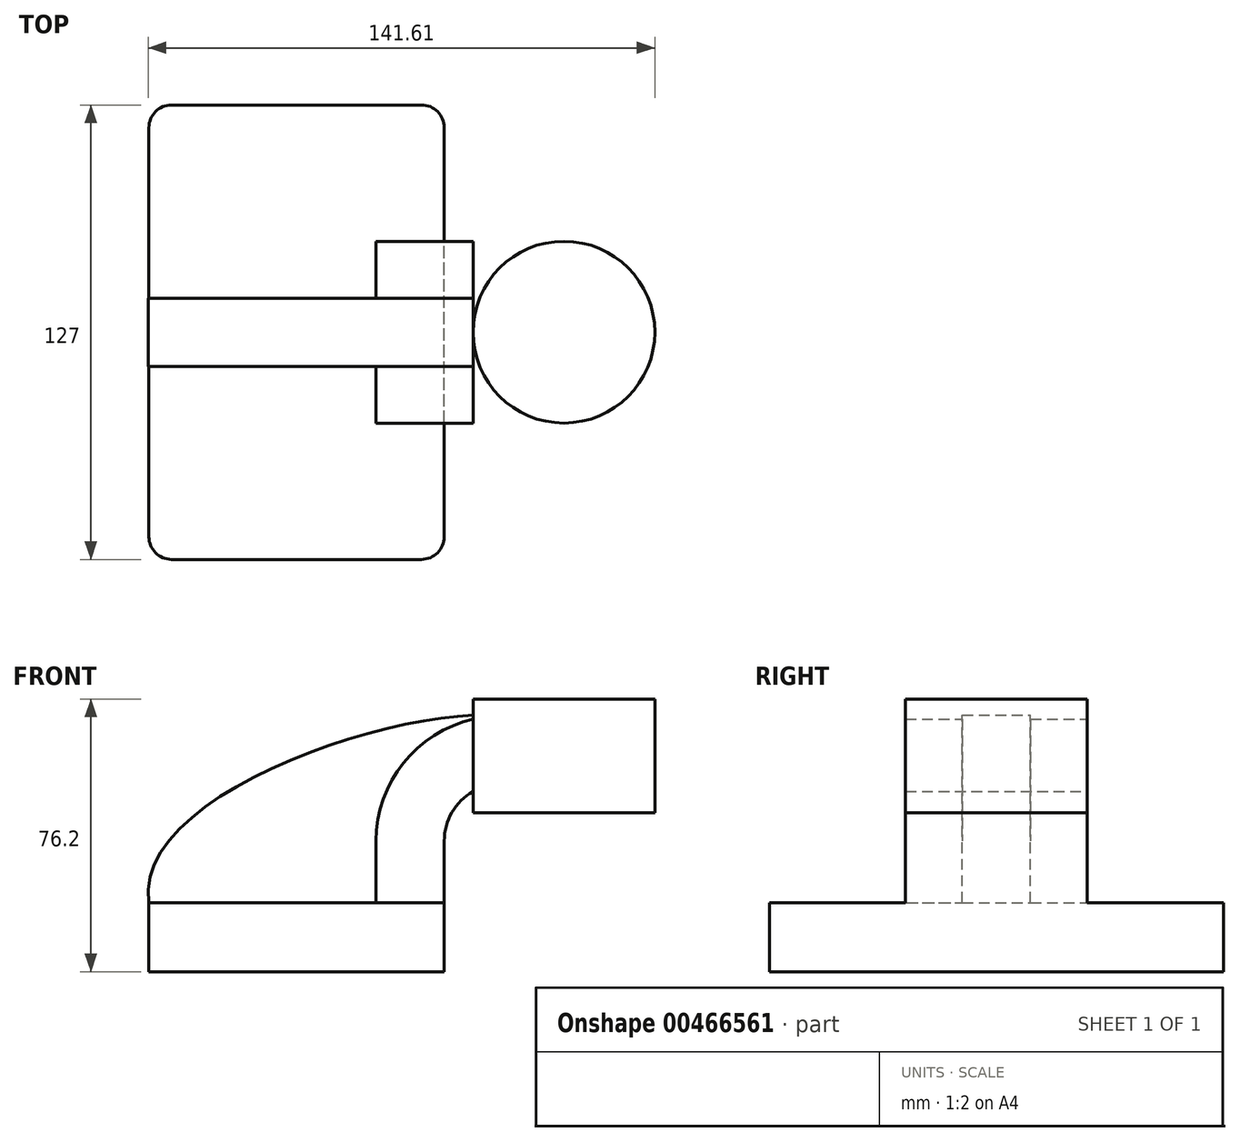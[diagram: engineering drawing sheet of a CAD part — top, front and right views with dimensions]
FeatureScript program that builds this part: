
annotation { "Feature Type Name" : "Feature", "Feature Type Description" : "" }
export const myFeature = defineFeature(function(context is Context, id is Id, definition is map)
    precondition{}
    {
        {
            var Q0;
            Q0=qCreatedBy(makeId("Front.planeOp"),FACE);
            var sketch = newSketch(context, id + "F0", { "sketchPlane" : qUnion([Q0])});
            skLineSegment(sketch, "E0.bottom", {"start": v(-41.28, 9.65) * mm, "end": v(41.27, 9.65) * mm});
            skLineSegment(sketch, "E0.top", {"start": v(-41.28, -9.65) * mm, "end": v(41.28, -9.65) * mm});
            skLineSegment(sketch, "E0.left", {"start": v(-41.28, 9.65) * mm, "end": v(-41.27, -9.65) * mm});
            skLineSegment(sketch, "E0.right", {"start": v(41.28, 9.65) * mm, "end": v(41.28, -9.65) * mm});
            skPoint(sketch, "E0.middle", {"position": v(0, 0) * mm});
            skLineSegment(sketch, "E1", {"start": v(41.27, 9.65) * mm, "end": v(41.27, 26.87) * mm});
            skLineSegment(sketch, "E2.bottom", {"start": v(49.31, 34.8) * mm, "end": v(100.11, 34.8) * mm});
            skLineSegment(sketch, "E2.top", {"start": v(49.31, 66.55) * mm, "end": v(100.11, 66.55) * mm});
            skLineSegment(sketch, "E2.left", {"start": v(49.31, 34.8) * mm, "end": v(49.31, 66.55) * mm});
            skLineSegment(sketch, "E2.right", {"start": v(100.11, 34.8) * mm, "end": v(100.11, 66.55) * mm});
            skPoint(sketch, "E2.middle", {"position": v(74.71, 50.67) * mm});
            skArc(sketch, "E3", {"start": v(41.27, 26.87) * mm, "mid": v(45.92, 38.1) * mm, "end": v(57.15, 42.75) * mm});
            skLineSegment(sketch, "E4", {"start": v(57.15, 42.75) * mm, "end": v(70.79, 42.75) * mm});
            skLineSegment(sketch, "E5.0", {"start": v(57.15, 61.8) * mm, "end": v(70.79, 61.8) * mm});
            skArc(sketch, "E5.1", {"start": v(22.22, 26.87) * mm, "mid": v(32.45, 51.57) * mm, "end": v(57.15, 61.8) * mm});
            skLineSegment(sketch, "E5.2", {"start": v(22.22, 9.65) * mm, "end": v(22.22, 26.87) * mm});
            skLineSegment(sketch, "E6", {"start": v(74.71, 34.8) * mm, "end": v(74.71, 66.55) * mm});
            skFitSpline(sketch, "E7", {"points": [v(-41.28, 9.65) * mm, v(57.15, 61.8) * mm], "startDerivative": vector(-14.58, 91.77) * mm, "endDerivative": vector(82.09, -9.41) * mm});
            skLineSegment(sketch, "E8", {"start": v(70.79, 61.8) * mm, "end": v(70.79, 42.75) * mm});
            skSolve(sketch);
        }
        {
            var Q0;
            Q0=makeQuery(id+"F0.imprint","IMPRINT",FACE,{"disambiguationData":[TD([[makeQuery(id+"F0.imprint","IMPRINT",EDGE,{"derivedFrom":sQuery(id+"F0.wireOp",EDGE,"E0.top")}),1.0]])]});
            extrude(context, id + "F1", {"entities" : qUnion([Q0]), "endBound" : BoundingType.SYMMETRIC, "depth" : 127 * mm});
        }
        {
            var Q0;
            {var subQ1=sQuery(id+"F0.wireOp",EDGE,"E1");Q0=makeQuery(id+"F0.imprint","IMPRINT",FACE,{"disambiguationData":[TD([[makeQuery(id+"F0.imprint","IMPRINT",EDGE,{"derivedFrom":subQ1}),1.0]])]});}
            extrude(context, id + "F2", {"entities" : qUnion([Q0]), "operationType" : NewBodyOperationType.ADD, "endBound" : BoundingType.SYMMETRIC, "depth" : 50.8 * mm});
        }
        {
            var Q0;
            {var subQ0=sQuery(id+"F0.wireOp",EDGE,"E5.2");Q0=makeQuery(id+"F0.imprint","IMPRINT",FACE,{"disambiguationData":[TD([[makeQuery(id+"F0.imprint","IMPRINT",EDGE,{"derivedFrom":subQ0}),1.0]])]});}
            extrude(context, id + "F3", {"entities" : qUnion([Q0]), "operationType" : NewBodyOperationType.ADD, "endBound" : BoundingType.SYMMETRIC, "depth" : 19.05 * mm});
        }
        {
            var Q0;
            {var subQ0=sQuery(id+"F0.wireOp",EDGE,"E2.right");Q0=makeQuery(id+"F0.imprint","IMPRINT",FACE,{"disambiguationData":[TD([[makeQuery(id+"F0.imprint","IMPRINT",EDGE,{"derivedFrom":subQ0}),1.0]])]});}
            var Q1;
            Q1=sQuery(id+"F0.wireOp",EDGE,"E6");
            revolve(context, id + "F4", {"operationType" : NewBodyOperationType.ADD, "entities" : qUnion([Q0]), "axis" : qUnion([Q1]), "revolveType" : RevolveType.FULL});
        }
        {
            var Q0;
            Q0=makeQuery(id+"F1.opExtrude","CAP_EDGE",EDGE,{"disambiguationData":[OSD([sQuery(id+"F0.wireOp",EDGE,"E0.right")])],"isStart":false});
            var Q1;
            Q1=makeQuery(id+"F1.opExtrude","CAP_EDGE",EDGE,{"disambiguationData":[OSD([sQuery(id+"F0.wireOp",EDGE,"E0.left")])],"isStart":false});
            var Q2;
            Q2=makeQuery(id+"F1.opExtrude","CAP_EDGE",EDGE,{"disambiguationData":[OSD([sQuery(id+"F0.wireOp",EDGE,"E0.left")])],"isStart":true});
            var Q3;
            Q3=makeQuery(id+"F1.opExtrude","CAP_EDGE",EDGE,{"disambiguationData":[OSD([sQuery(id+"F0.wireOp",EDGE,"E0.right")])],"isStart":true});
            fillet(context, id + "F5", {"entities" : qUnion([Q0, Q1, Q2, Q3]), "radius" : 6.35 * mm, "tangentPropagation" : true, "allowEdgeOverflow" : false});
        }
    });
